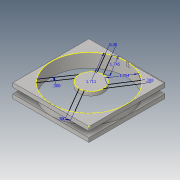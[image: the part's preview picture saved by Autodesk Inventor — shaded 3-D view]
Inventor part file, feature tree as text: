
AUTODESK INVENTOR PART (.ipt)
format: ipt  version: 2016 (Build 200138000, 138)  size: 212,480 bytes
history: native  units: in
note: dims shown in document units (in); Inventor stores cm internally (conversion verified against a paired STEP export)
features: sketch x13, extrude x10
ambient origin geometry x8: Origin, YZ Plane, XZ Plane, XY Plane, X Axis, Y Axis, Z Axis, Center Point
bodies: Solid1 (feature_tree)
feature tree (23):
  extrude  "Extrusion1"  Depth=5.5in
  extrude  "Extrusion2"  Depth=0.3in TaperAngle=0.0deg
  extrude  "Extrusion3"  Depth=5.4in
  extrude  "Extrusion4"  Depth=0.05in
  extrude  "Extrusion5"  Depth=5.5in
  extrude  "Extrusion6"  Depth=2.75in
  extrude  "Extrusion7"  Depth=5.5in
  extrude  "Extrusion8"  Depth=5.5in
  extrude  "Extrusion9"  Depth=0.05in
  extrude  "Extrusion10"  Depth=0.3in TaperAngle=0.0deg
  sketch  "Sketch11"  dims[d24=5.4in]
  sketch  "Sketch12"  dims[d25=2.75in]
  sketch  "Sketch13"  dims[d26=2.75in d27=1.0in d28=0.0in d29=1.75in d30=2.75in d31=0.3in d32=0.0in d33=0.3in d34=0.0in d35=0.3in d36=0.0in d37=0.3in d38=0.0in d39=0.3in d40=0.0in d41=0.3in d42=0.3in d43=1.7111in d44=1.7446in d45=1.7542in d46=0.0021in d47=0.3in]
  sketch  "Sketch1"  dims[d0=5.5in d1=5.5in]
  sketch  "Sketch2"  dims[d2=5.5in d3=0.3in d4=0.0in]
  sketch  "Sketch3"  dims[d5=5.4in d6=5.4in]
  sketch  "Sketch4"  dims[d7=0.05in d8=0.05in]
  sketch  "Sketch5"  dims[d9=1.0in d10=0.0in d11=5.5in]
  sketch  "Sketch6"  dims[d12=2.75in d13=2.75in]
  sketch  "Sketch7"  dims[d14=0.4in d15=0.0in d16=5.5in]
  sketch  "Sketch8"  dims[d17=5.5in d18=5.4in]
  sketch  "Sketch9"  dims[d19=5.4in d20=0.05in]
  sketch  "Sketch10"  dims[d21=0.05in d22=0.3in d23=0.0in]
